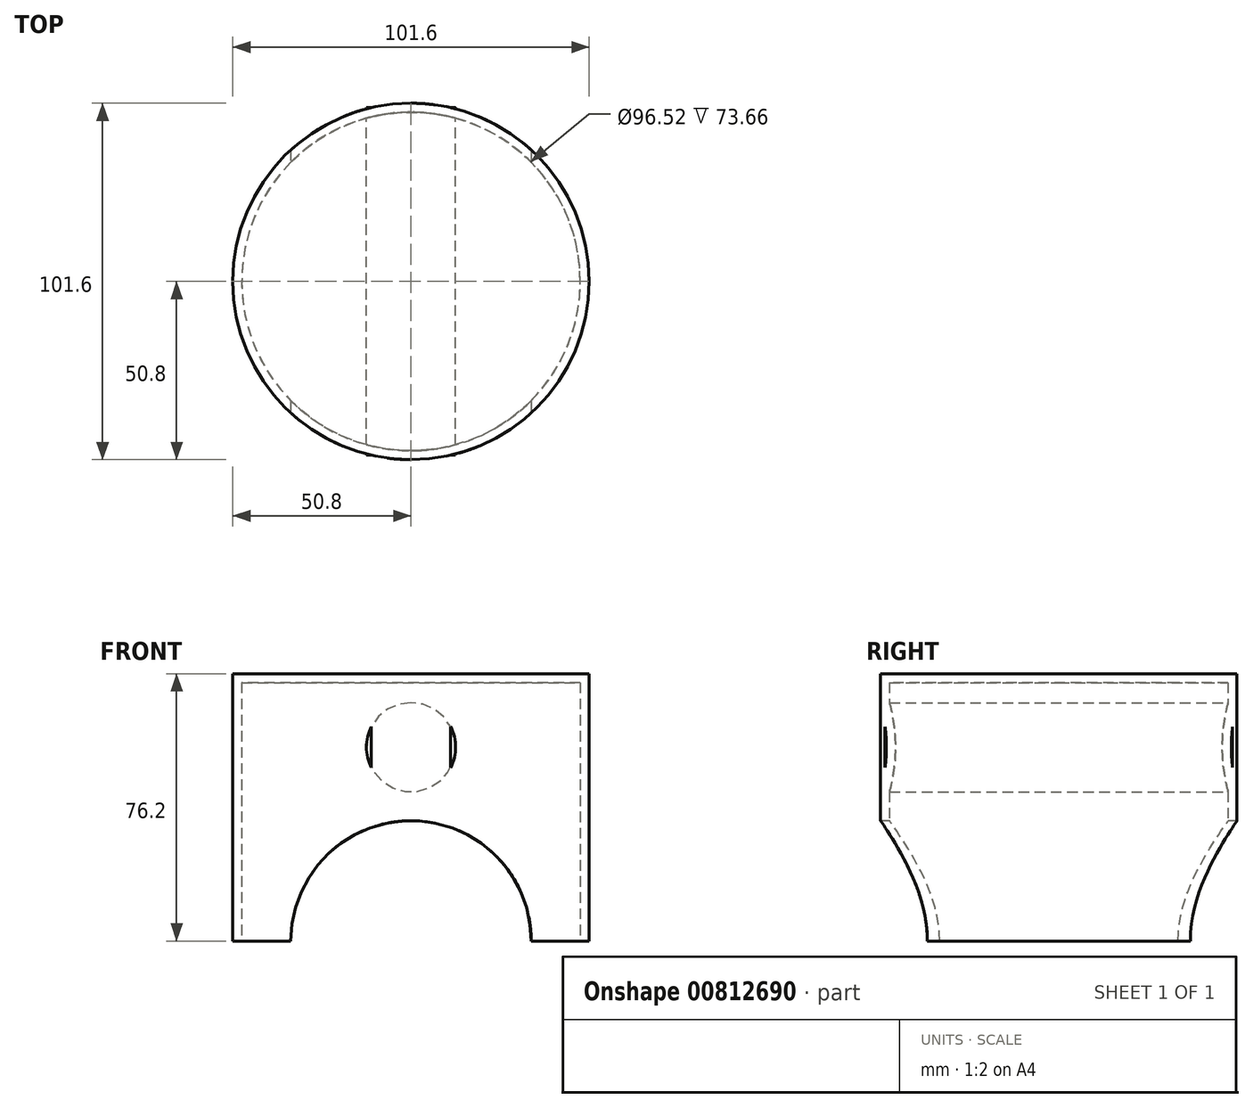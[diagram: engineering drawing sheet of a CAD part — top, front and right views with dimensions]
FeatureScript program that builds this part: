
annotation { "Feature Type Name" : "Feature", "Feature Type Description" : "" }
export const myFeature = defineFeature(function(context is Context, id is Id, definition is map)
    precondition{}
    {
        {
            var Q0;
            Q0=qCreatedBy(makeId("Front.planeOp"),FACE);
            var sketch = newSketch(context, id + "F0", { "sketchPlane" : qUnion([Q0])});
            skLineSegment(sketch, "E0.bottom", {"start": v(25.4, -38.1) * mm, "end": v(-25.4, -38.1) * mm});
            skLineSegment(sketch, "E0.top", {"start": v(25.4, 38.1) * mm, "end": v(-25.4, 38.1) * mm});
            skLineSegment(sketch, "E0.left", {"start": v(25.4, -38.1) * mm, "end": v(25.4, 38.1) * mm});
            skLineSegment(sketch, "E0.right", {"start": v(-25.4, -38.1) * mm, "end": v(-25.4, 38.1) * mm});
            skPoint(sketch, "E0.middle", {"position": v(0, 0) * mm});
            skSolve(sketch);
        }
        {
            var Q0;
            Q0=makeQuery(id+"F0.imprint","IMPRINT",FACE,{"disambiguationData":[TD([[makeQuery(id+"F0.imprint","IMPRINT",EDGE,{"derivedFrom":sQuery(id+"F0.wireOp",EDGE,"E0.bottom")}),-1.0]])]});
            var Q1;
            Q1=sQuery(id+"F0.wireOp",EDGE,"E0.right");
            revolve(context, id + "F1", {"surfaceOperationType" : NewSurfaceOperationType.NEW, "entities" : qUnion([Q0]), "axis" : qUnion([Q1]), "revolveType" : RevolveType.FULL});
        }
        {
            var Q0;
            Q0=makeQuery(id+"F1.opRevolve","SWEPT_FACE",FACE,{"disambiguationData":[OSD([sQuery(id+"F0.wireOp",EDGE,"E0.bottom")])]});
            shell(context, id + "F2", {"entities" : qUnion([Q0]), "thickness" : 2.54 * mm});
        }
        {
            var Q0;
            Q0=qCreatedBy(makeId("Front.planeOp"),FACE);
            var sketch = newSketch(context, id + "F3", { "sketchPlane" : qUnion([Q0])});
            skLineSegment(sketch, "E1.0", {"start": v(25.4, -38.1) * mm, "end": v(-76.2, -38.1) * mm, "construction": true});
            skArc(sketch, "E2", {"start": v(-59.67, -38.1) * mm, "mid": v(-25.4, -3.83) * mm, "end": v(8.87, -38.1) * mm});
            skLineSegment(sketch, "E3", {"start": v(-59.67, -38.1) * mm, "end": v(8.87, -38.1) * mm});
            skSolve(sketch);
        }
        {
            var Q0;
            Q0 = qSketchRegion(id + "F3", true);
            extrude(context, id + "F4", {"entities" : qUnion([Q0]), "operationType" : NewBodyOperationType.REMOVE, "endBound" : BoundingType.SYMMETRIC, "oppositeDirection" : true, "depth" : 121.92 * mm, "offsetDistance" : 25.4 * mm});
        }
        {
            var Q0;
            Q0=qCreatedBy(makeId("Front.planeOp"),FACE);
            var sketch = newSketch(context, id + "F5", { "sketchPlane" : qUnion([Q0])});
            skArc(sketch, "E4.0", {"start": v(8.87, -38.1) * mm, "mid": v(-25.4, -3.83) * mm, "end": v(-59.67, -38.1) * mm, "construction": true});
            skCircle(sketch, "E5", {"center": v(-25.4, 17.15) * mm, "radius": 12.7 * mm});
            skPoint(sketch, "E5.centerSnap0", {"position": v(-25.4, -3.83) * mm});
            skSolve(sketch);
        }
        {
            var Q0;
            Q0 = qSketchRegion(id + "F5", true);
            extrude(context, id + "F6", {"entities" : qUnion([Q0]), "operationType" : NewBodyOperationType.ADD, "endBound" : BoundingType.SYMMETRIC, "depth" : 99.06 * mm, "offsetDistance" : 25.4 * mm});
        }
    });
